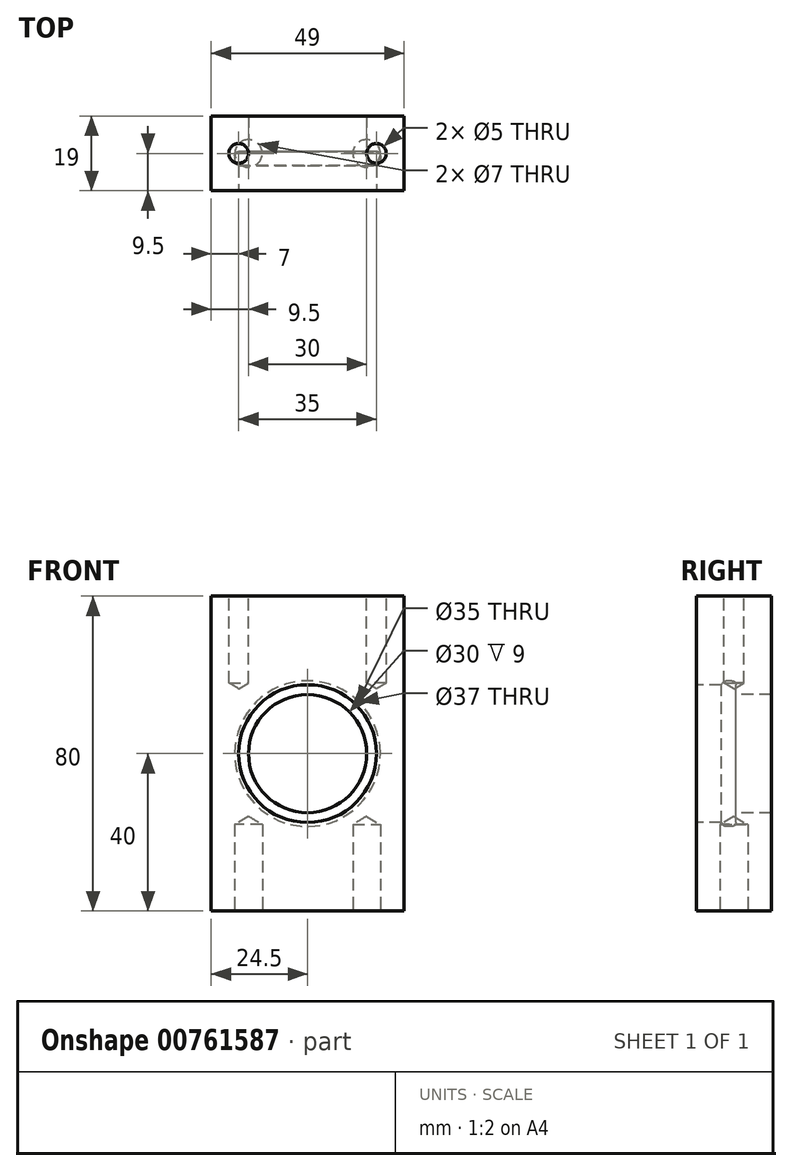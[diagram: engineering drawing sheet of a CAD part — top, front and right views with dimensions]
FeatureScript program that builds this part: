
annotation { "Feature Type Name" : "Feature", "Feature Type Description" : "" }
export const myFeature = defineFeature(function(context is Context, id is Id, definition is map)
    precondition{}
    {
        {
            var Q0;
            Q0=qCreatedBy(makeId("Front.planeOp"),FACE);
            var sketch = newSketch(context, id + "F0", { "sketchPlane" : qUnion([Q0])});
            skLineSegment(sketch, "E0.bottom", {"start": v(0, 40) * mm, "end": v(24.5, 40) * mm});
            skLineSegment(sketch, "E0.top", {"start": v(0, -40) * mm, "end": v(24.5, -40) * mm});
            skLineSegment(sketch, "E0.left", {"start": v(0, 40) * mm, "end": v(0, -40) * mm});
            skLineSegment(sketch, "E0.right", {"start": v(24.5, 40) * mm, "end": v(24.5, -40) * mm});
            skPoint(sketch, "E0.middle", {"position": v(12.25, 0) * mm});
            skSolve(sketch);
        }
        {
            var Q0;
            Q0 = qSketchRegion(id + "F0", true);
            extrude(context, id + "F1", {"entities" : qUnion([Q0]), "endBound" : BoundingType.SYMMETRIC, "depth" : 19 * mm, "offsetDistance" : 25 * mm});
        }
        {
            var Q0;
            Q0=makeQuery(id+"F1.opExtrude","SWEPT_FACE",FACE,{"disambiguationData":[OSD([sQuery(id+"F0.wireOp",EDGE,"E0.bottom")])]});
            var sketch = newSketch(context, id + "F2", { "sketchPlane" : qUnion([Q0])});
            skPoint(sketch, "E1", {"position": v(17.5, 0) * mm});
            skSolve(sketch);
        }
        {
            var Q0;
            Q0=sQuery(id+"F2.wireOp",VERTEX,"E1");
            var Q1;
            Q1=makeQuery(id+"F1.opExtrude","SWEPT_BODY",BODY,{"disambiguationData":[OSD([sQuery(id+"F0.wireOp",EDGE,"E0.bottom"),sQuery(id+"F0.wireOp",EDGE,"E0.top"),sQuery(id+"F0.wireOp",EDGE,"E0.left"),sQuery(id+"F0.wireOp",EDGE,"E0.right")])]});
            hole(context, id + "F3", {"style" : HoleStyle.SIMPLE, "endStyle" : HoleEndStyle.BLIND, "standardTappedOrClearance" : lookupTablePath({ "standard" : "ISO", "engagement" : "75%", "pitch" : "1 mm", "size" : "M6", "type" : "Tapped" }), "standardBlindInLast" : lookupTablePath({ "standard" : "ISO", "engagement" : "75%", "pitch" : "1 mm", "size" : "M6", "type" : "Tapped" }), "holeDiameter" : 5 * mm, "majorDiameter" : 6 * mm, "showTappedDepth" : true, "holeDepth" : 22 * mm, "isTappedThrough" : true, "tappedDepth" : 18 * mm, "tapClearance" : 4, "startFromSketch" : true, "locations" : qUnion([Q0]), "scope" : qUnion([Q1])});
        }
        {
            var Q0;
            Q0=makeQuery(id+"F1.opExtrude","SWEPT_FACE",FACE,{"disambiguationData":[OSD([sQuery(id+"F0.wireOp",EDGE,"E0.top")])]});
            var sketch = newSketch(context, id + "F4", { "sketchPlane" : qUnion([Q0])});
            skPoint(sketch, "E2", {"position": v(15, 0) * mm});
            skSolve(sketch);
        }
        {
            var Q0;
            Q0=sQuery(id+"F4.wireOp",VERTEX,"E2");
            var Q1;
            Q1=makeQuery(id+"F1.opExtrude","SWEPT_BODY",BODY,{"disambiguationData":[OSD([sQuery(id+"F0.wireOp",EDGE,"E0.bottom"),sQuery(id+"F0.wireOp",EDGE,"E0.top"),sQuery(id+"F0.wireOp",EDGE,"E0.left"),sQuery(id+"F0.wireOp",EDGE,"E0.right")])]});
            hole(context, id + "F5", {"style" : HoleStyle.SIMPLE, "endStyle" : HoleEndStyle.BLIND, "standardTappedOrClearance" : lookupTablePath({ "standard" : "ISO", "engagement" : "75%", "pitch" : "1 mm", "size" : "M8", "type" : "Tapped" }), "standardBlindInLast" : lookupTablePath({ "standard" : "ISO", "engagement" : "75%", "pitch" : "1 mm", "size" : "M8", "type" : "Tapped" }), "holeDiameter" : 7 * mm, "majorDiameter" : 8 * mm, "showTappedDepth" : true, "holeDepth" : 22 * mm, "isTappedThrough" : true, "tappedDepth" : 18 * mm, "tapClearance" : 4, "startFromSketch" : true, "locations" : qUnion([Q0]), "scope" : qUnion([Q1])});
        }
        {
            var Q0;
            Q0=qCreatedBy(makeId("Right.planeOp"),FACE);
            var sketch = newSketch(context, id + "F6", { "sketchPlane" : qUnion([Q0])});
            skLineSegment(sketch, "E3", {"start": v(9.5, 0) * mm, "end": v(9.5, 15) * mm});
            skLineSegment(sketch, "E4", {"start": v(9.5, 15) * mm, "end": v(0.5, 15) * mm});
            skLineSegment(sketch, "E5", {"start": v(0.5, 15) * mm, "end": v(0.5, 17.5) * mm});
            skLineSegment(sketch, "E6", {"start": v(-0.5, 18.5) * mm, "end": v(-2, 18.5) * mm});
            skLineSegment(sketch, "E7", {"start": v(-2.87, 18) * mm, "end": v(-3.15, 17.5) * mm});
            skLineSegment(sketch, "E8", {"start": v(-3.15, 17.5) * mm, "end": v(-9.5, 17.5) * mm});
            skLineSegment(sketch, "E9", {"start": v(-9.5, 17.5) * mm, "end": v(-9.5, 0) * mm});
            skLineSegment(sketch, "E10", {"start": v(-9.5, 0) * mm, "end": v(9.5, 0) * mm});
            skPoint(sketch, "E11.visualSharp", {"position": v(-2.58, 18.5) * mm});
            skArc(sketch, "E11.filletArc", {"start": v(-2, 18.5) * mm, "mid": v(-2.5, 18.37) * mm, "end": v(-2.87, 18) * mm});
            skPoint(sketch, "E12.visualSharp", {"position": v(0.5, 18.5) * mm});
            skArc(sketch, "E12.filletArc", {"start": v(0.5, 17.5) * mm, "mid": v(0.2, 18.2) * mm, "end": v(-0.5, 18.5) * mm});
            skSolve(sketch);
        }
        {
            var Q0;
            Q0=makeQuery(id+"F6.imprint","IMPRINT",FACE,{"disambiguationData":[TD([[makeQuery(id+"F6.imprint","IMPRINT",EDGE,{"derivedFrom":sQuery(id+"F6.wireOp",EDGE,"E3")}),1.0]])]});
            var Q1;
            Q1=sQuery(id+"F6.wireOp",EDGE,"E10");
            revolve(context, id + "F7", {"operationType" : NewBodyOperationType.REMOVE, "surfaceOperationType" : NewSurfaceOperationType.NEW, "entities" : qUnion([Q0]), "axis" : qUnion([Q1]), "revolveType" : RevolveType.ONE_DIRECTION, "angle" : 180 * degree});
        }
        {
            var Q0;
            Q0=makeQuery(id+"F1.opExtrude","SWEPT_BODY",BODY,{"disambiguationData":[OSD([sQuery(id+"F0.wireOp",EDGE,"E0.bottom"),sQuery(id+"F0.wireOp",EDGE,"E0.top"),sQuery(id+"F0.wireOp",EDGE,"E0.left"),sQuery(id+"F0.wireOp",EDGE,"E0.right")])]});
            var Q1;
            Q1=qCreatedBy(makeId("Right.planeOp"),FACE);
            mirror(context, id + "F8", {"operationType" : NewBodyOperationType.ADD, "entities" : qUnion([Q0]), "mirrorPlane" : qUnion([Q1])});
        }
    });
